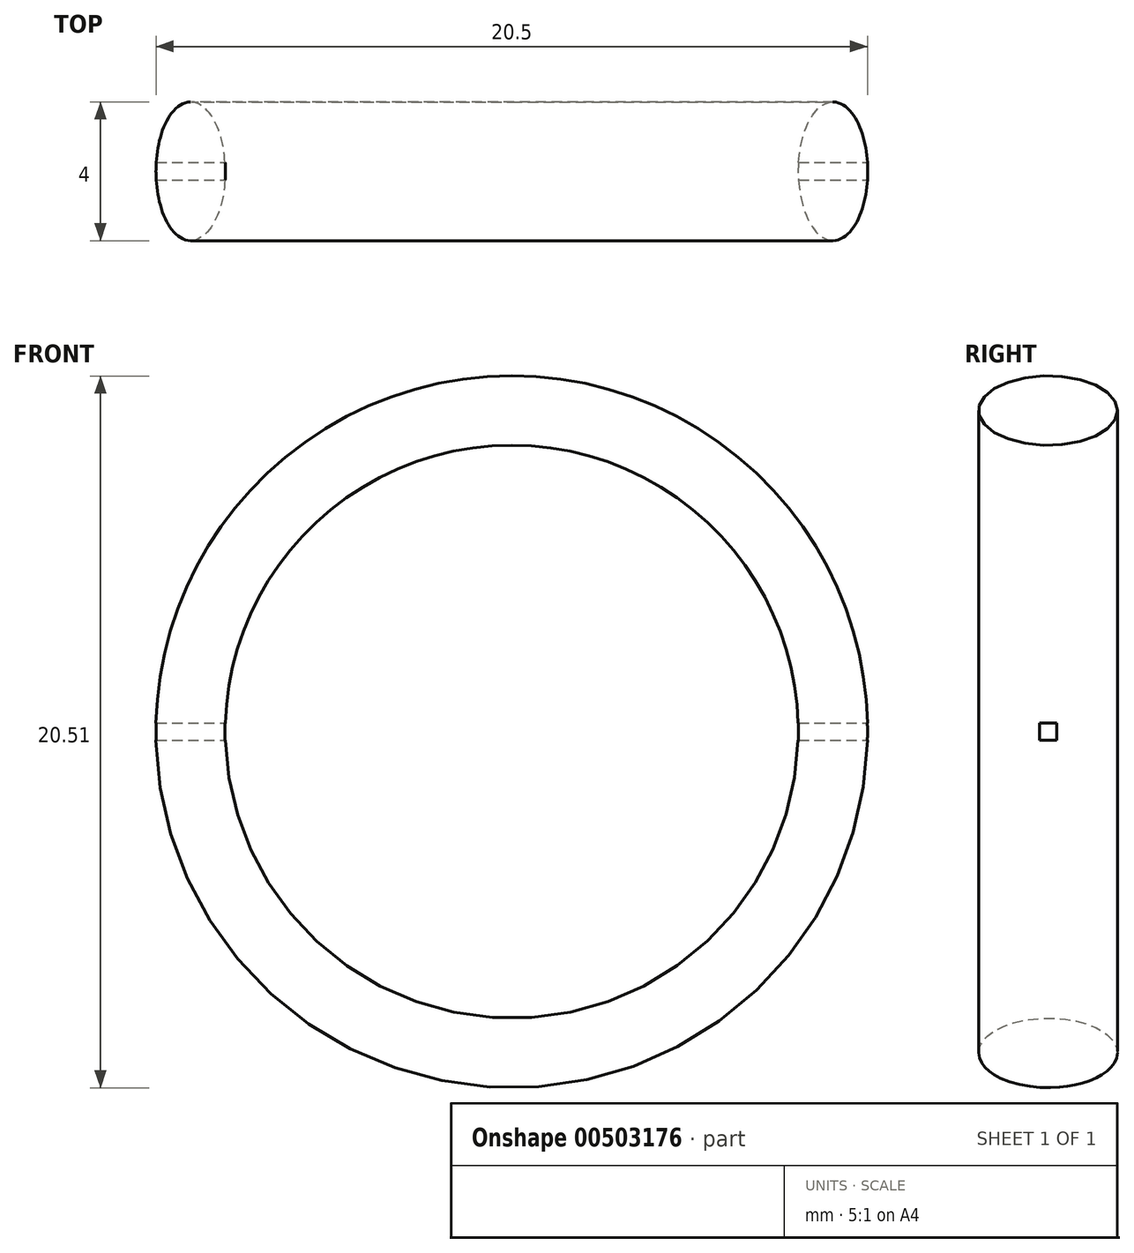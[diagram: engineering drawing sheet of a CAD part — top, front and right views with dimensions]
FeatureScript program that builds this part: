
annotation { "Feature Type Name" : "Feature", "Feature Type Description" : "" }
export const myFeature = defineFeature(function(context is Context, id is Id, definition is map)
    precondition{}
    {
        {
            var Q0;
            Q0=qCreatedBy(makeId("Front.planeOp"),FACE);
            var sketch = newSketch(context, id + "F0", { "sketchPlane" : qUnion([Q0])});
            skArc(sketch, "E0", {"start": v(-8.26, 0) * mm, "mid": v(0, -8.26) * mm, "end": v(8.26, 0) * mm});
            skArc(sketch, "E1", {"start": v(-8.63, 0) * mm, "mid": v(0, -8.63) * mm, "end": v(8.63, 0) * mm});
            skLineSegment(sketch, "E2", {"start": v(-8.63, 0) * mm, "end": v(8.63, 0) * mm});
            skSolve(sketch);
        }
        {
            var Q0;
            Q0=qCreatedBy(makeId("Top.planeOp"),FACE);
            var sketch = newSketch(context, id + "F1", { "sketchPlane" : qUnion([Q0])});
            skLineSegment(sketch, "E3", {"start": v(0, 3.67) * mm, "end": v(0, -7.56) * mm});
            skEllipse(sketch, "E4", {"center": v(9.25, 0) * mm, "majorRadius": 1 * mm, "minorRadius": 2 * mm, "majorAxis": v(-1, 0)});
            skSolve(sketch);
        }
        {
            var Q0;
            Q0 = qSketchRegion(id + "F1", true);
            var Q1;
            Q1=sQuery(id+"F1.wireOp",EDGE,"E3");
            revolve(context, id + "F2", {"entities" : qUnion([Q0]), "axis" : qUnion([Q1]), "revolveType" : RevolveType.FULL});
        }
        {
            var Q0;
            Q0=qCreatedBy(makeId("Right.planeOp"),FACE);
            var sketch = newSketch(context, id + "F3", { "sketchPlane" : qUnion([Q0])});
            skLineSegment(sketch, "E5.bottom", {"start": v(0.25, 0.25) * mm, "end": v(-0.25, 0.25) * mm});
            skLineSegment(sketch, "E5.top", {"start": v(0.25, -0.25) * mm, "end": v(-0.25, -0.25) * mm});
            skLineSegment(sketch, "E5.left", {"start": v(0.25, 0.25) * mm, "end": v(0.25, -0.25) * mm});
            skLineSegment(sketch, "E5.right", {"start": v(-0.25, 0.25) * mm, "end": v(-0.25, -0.25) * mm});
            skPoint(sketch, "E5.middle", {"position": v(0, 0) * mm});
            skSolve(sketch);
        }
        {
            var Q0;
            Q0=makeQuery(id+"F3.imprint","IMPRINT",FACE,{"disambiguationData":[TD([[makeQuery(id+"F3.imprint","IMPRINT",EDGE,{"derivedFrom":sQuery(id+"F3.wireOp",EDGE,"E5.bottom")}),1.0]])]});
            extrude(context, id + "F4", {"entities" : qUnion([Q0]), "operationType" : NewBodyOperationType.REMOVE, "endBound" : BoundingType.THROUGH_ALL, "oppositeDirection" : true, "depth" : 25.4 * mm, "offsetDistance" : 25.4 * mm, "hasSecondDirection" : true, "secondDirectionBound" : SecondDirectionBoundingType.THROUGH_ALL, "secondDirectionOppositeDirection" : false, "secondDirectionDepth" : 25.4 * mm});
        }
    });
